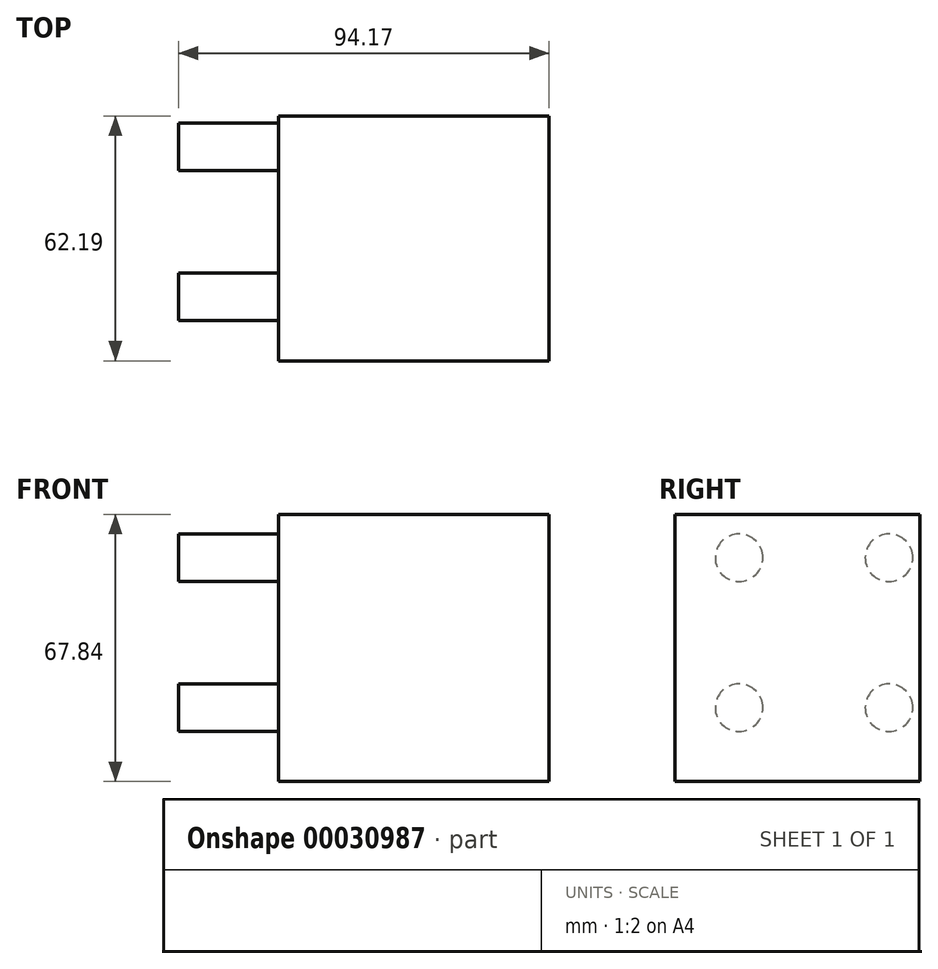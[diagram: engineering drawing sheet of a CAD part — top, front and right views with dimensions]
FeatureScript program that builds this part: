
annotation { "Feature Type Name" : "Feature", "Feature Type Description" : "" }
export const myFeature = defineFeature(function(context is Context, id is Id, definition is map)
    precondition{}
    {
        {
            var Q0;
            Q0=qCreatedBy(makeId("Top.planeOp"),FACE);
            var sketch = newSketch(context, id + "F0", { "sketchPlane" : qUnion([Q0])});
            skLineSegment(sketch, "E0.bottom", {"start": v(-33.44, -28.36) * mm, "end": v(35.33, -28.36) * mm});
            skLineSegment(sketch, "E0.top", {"start": v(-33.44, 33.83) * mm, "end": v(35.33, 33.83) * mm});
            skLineSegment(sketch, "E0.left", {"start": v(-33.44, -28.36) * mm, "end": v(-33.44, 33.83) * mm});
            skLineSegment(sketch, "E0.right", {"start": v(35.33, -28.36) * mm, "end": v(35.33, 33.83) * mm});
            skSolve(sketch);
        }
        {
            var Q0;
            Q0 = qSketchRegion(id + "F0", true);
            extrude(context, id + "F1", {"entities" : qUnion([Q0]), "depth" : 67.84 * mm});
        }
        {
            var Q0;
            Q0=makeQuery(id+"F1.opExtrude","SWEPT_FACE",FACE,{"disambiguationData":[OSD([sQuery(id+"F0.wireOp",EDGE,"E0.left")])]});
            var sketch = newSketch(context, id + "F2", { "sketchPlane" : qUnion([Q0])});
            skCircle(sketch, "E1", {"center": v(-26, 56.84) * mm, "radius": 6.05 * mm});
            skCircle(sketch, "E2", {"center": v(-26, 18.74) * mm, "radius": 6.05 * mm});
            skCircle(sketch, "E3", {"center": v(12.1, 56.84) * mm, "radius": 6.05 * mm});
            skCircle(sketch, "E4", {"center": v(12.1, 18.74) * mm, "radius": 6.05 * mm});
            skSolve(sketch);
        }
        {
            var Q0;
            Q0 = qSketchRegion(id + "F2", true);
            extrude(context, id + "F3", {"entities" : qUnion([Q0]), "operationType" : NewBodyOperationType.ADD, "depth" : 25.4 * mm});
        }
    });
